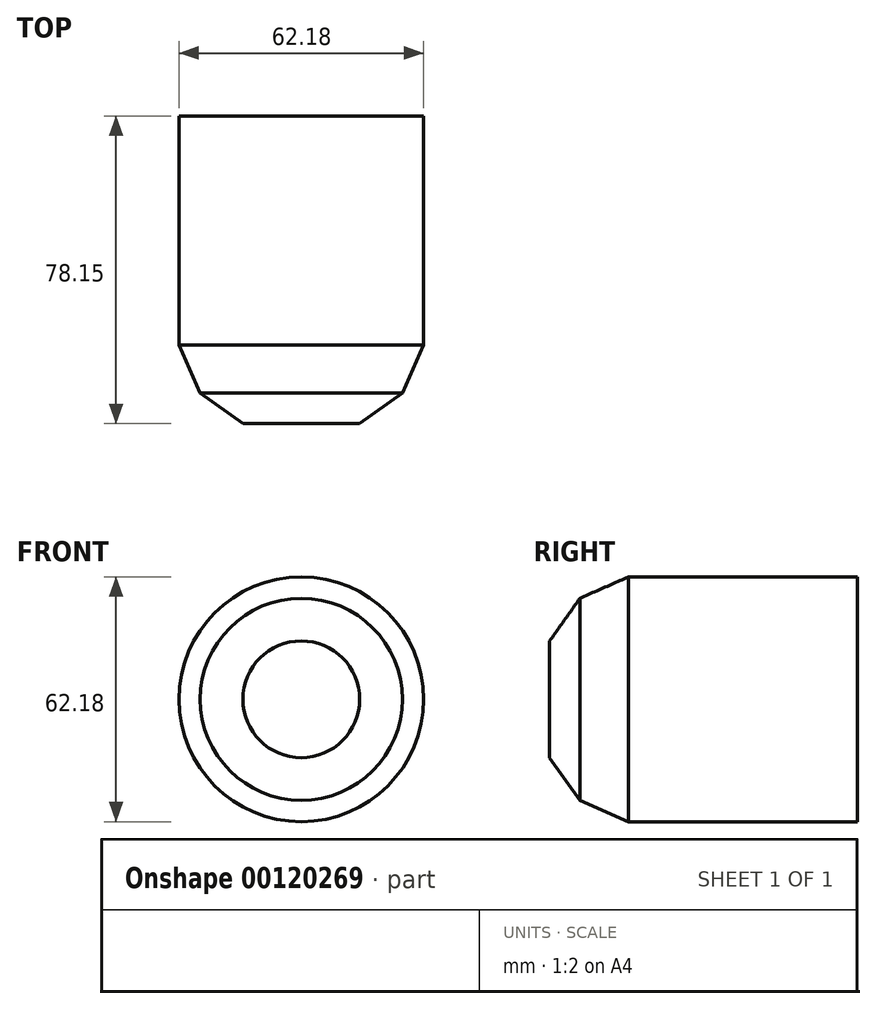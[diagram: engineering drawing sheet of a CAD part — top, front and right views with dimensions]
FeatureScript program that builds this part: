
annotation { "Feature Type Name" : "Feature", "Feature Type Description" : "" }
export const myFeature = defineFeature(function(context is Context, id is Id, definition is map)
    precondition{}
    {
        {
            var Q0;
            Q0=qCreatedBy(makeId("Top.planeOp"),FACE);
            var sketch = newSketch(context, id + "F0", { "sketchPlane" : qUnion([Q0])});
            skLineSegment(sketch, "E0", {"start": v(-18.26, -44.35) * mm, "end": v(14.83, -44.35) * mm});
            skLineSegment(sketch, "E1", {"start": v(14.83, -44.35) * mm, "end": v(25.67, -36.65) * mm});
            skLineSegment(sketch, "E2", {"start": v(25.67, -36.65) * mm, "end": v(31.1, -24.39) * mm});
            skLineSegment(sketch, "E3", {"start": v(31.1, -24.39) * mm, "end": v(31.1, 33.8) * mm});
            skLineSegment(sketch, "E4", {"start": v(31.1, 33.8) * mm, "end": v(0, 33.8) * mm});
            skLineSegment(sketch, "E5", {"start": v(0, 33.8) * mm, "end": v(0, -44.35) * mm});
            skSolve(sketch);
        }
        {
            var Q0;
            {var subQ0=sQuery(id+"F0.wireOp",EDGE,"E1");Q0=makeQuery(id+"F0.imprint","IMPRINT",FACE,{"disambiguationData":[TD([[makeQuery(id+"F0.imprint","IMPRINT",EDGE,{"derivedFrom":subQ0}),1.0]])]});}
            var Q1;
            Q1=sQuery(id+"F0.wireOp",EDGE,"E5");
            revolve(context, id + "F1", {"entities" : qUnion([Q0]), "axis" : qUnion([Q1]), "revolveType" : RevolveType.FULL});
        }
    });
